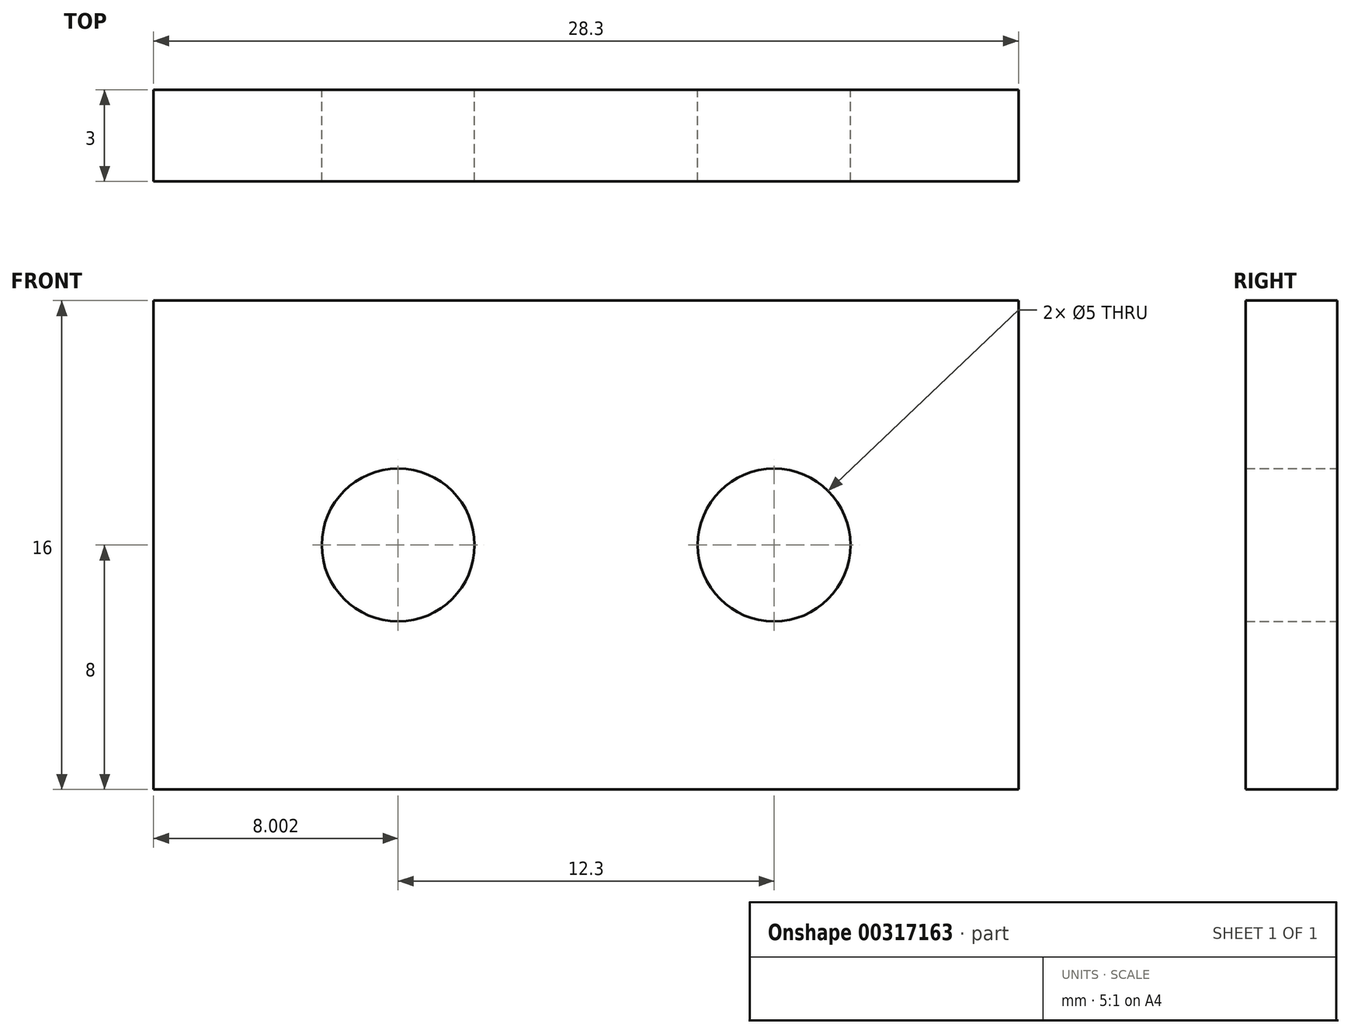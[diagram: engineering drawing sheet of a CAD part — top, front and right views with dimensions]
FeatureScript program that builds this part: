
annotation { "Feature Type Name" : "Feature", "Feature Type Description" : "" }
export const myFeature = defineFeature(function(context is Context, id is Id, definition is map)
    precondition{}
    {
        {
            var Q0;
            Q0=qCreatedBy(makeId("Front.planeOp"),FACE);
            var sketch = newSketch(context, id + "F0", { "sketchPlane" : qUnion([Q0])});
            skLineSegment(sketch, "E0.bottom", {"start": v(-9.66, 16.85) * mm, "end": v(18.64, 16.85) * mm});
            skLineSegment(sketch, "E0.top", {"start": v(-9.66, 0.85) * mm, "end": v(18.64, 0.85) * mm});
            skLineSegment(sketch, "E0.left", {"start": v(-9.66, 16.85) * mm, "end": v(-9.66, 0.85) * mm});
            skLineSegment(sketch, "E0.right", {"start": v(18.64, 16.85) * mm, "end": v(18.64, 0.85) * mm});
            skCircle(sketch, "E1", {"center": v(-1.66, 8.85) * mm, "radius": 2.5 * mm});
            skCircle(sketch, "E2", {"center": v(10.64, 8.85) * mm, "radius": 2.5 * mm});
            skSolve(sketch);
        }
        {
            var Q0;
            Q0 = qSketchRegion(id + "F0", true);
            extrude(context, id + "F1", {"entities" : qUnion([Q0]), "depth" : 3 * mm});
        }
    });
